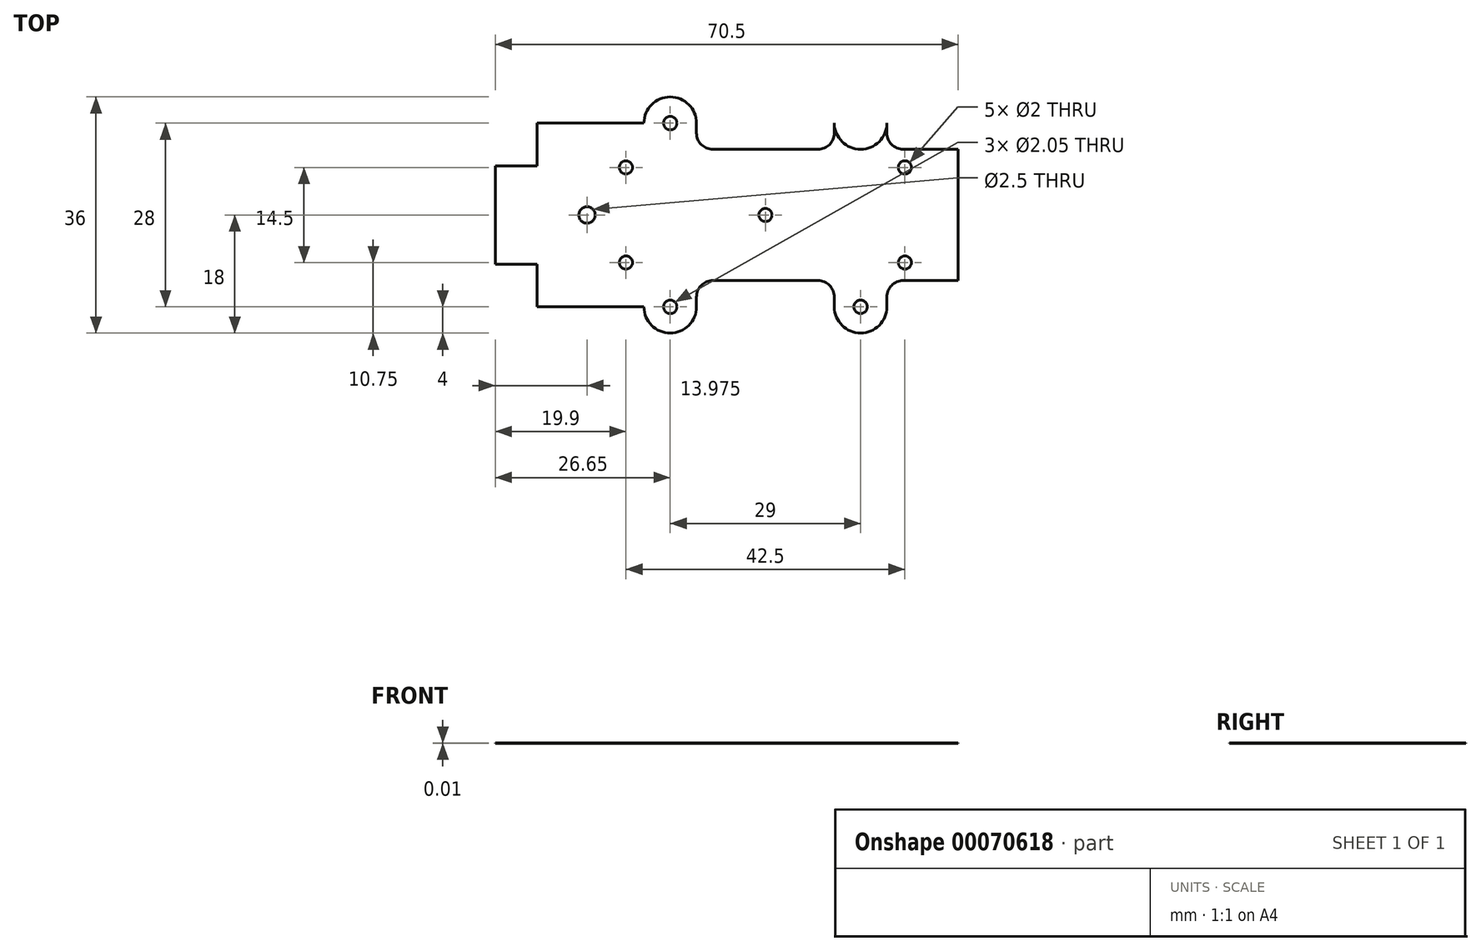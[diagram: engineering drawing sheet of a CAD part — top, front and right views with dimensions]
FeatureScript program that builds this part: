
annotation { "Feature Type Name" : "Feature", "Feature Type Description" : "" }
export const myFeature = defineFeature(function(context is Context, id is Id, definition is map)
    precondition{}
    {
        {
            var Q0;
            Q0=qCreatedBy(makeId("Top.planeOp"),FACE);
            var sketch = newSketch(context, id + "F0", { "sketchPlane" : qUnion([Q0])});
            skLineSegment(sketch, "E0.bottom", {"start": v(-34.8, 10) * mm, "end": v(29.35, 10) * mm});
            skLineSegment(sketch, "E0.top", {"start": v(-34.8, -10) * mm, "end": v(29.35, -10) * mm});
            skLineSegment(sketch, "E0.left", {"start": v(-34.8, 10) * mm, "end": v(-34.8, -10) * mm});
            skLineSegment(sketch, "E0.right", {"start": v(29.35, 10) * mm, "end": v(29.35, -10) * mm});
            skLineSegment(sketch, "E1.bottom", {"start": v(-41.15, 7.5) * mm, "end": v(-34.8, 7.5) * mm});
            skLineSegment(sketch, "E1.top", {"start": v(-41.15, -7.5) * mm, "end": v(-34.8, -7.5) * mm});
            skLineSegment(sketch, "E1.left", {"start": v(-41.15, 7.5) * mm, "end": v(-41.15, -7.5) * mm});
            skLineSegment(sketch, "E1.right", {"start": v(-34.8, 7.5) * mm, "end": v(-34.8, -7.5) * mm});
            skCircle(sketch, "E2", {"center": v(-14.5, 14) * mm, "radius": 4 * mm});
            skLineSegment(sketch, "E3", {"start": v(-18.5, 14) * mm, "end": v(-10.5, 14) * mm});
            skLineSegment(sketch, "E4.top", {"start": v(-18.5, 10) * mm, "end": v(-10.5, 10) * mm});
            skLineSegment(sketch, "E4.left", {"start": v(-18.5, 14) * mm, "end": v(-18.5, 10) * mm});
            skLineSegment(sketch, "E4.right", {"start": v(-10.5, 14) * mm, "end": v(-10.5, 10) * mm});
            skLineSegment(sketch, "E5.MirrorCS", {"start": v(18.5, 14) * mm, "end": v(18.5, 10) * mm});
            skLineSegment(sketch, "E6.MirrorCS", {"start": v(10.5, 14) * mm, "end": v(10.5, 10) * mm});
            skLineSegment(sketch, "E7.MirrorCS", {"start": v(18.5, 10) * mm, "end": v(10.5, 10) * mm});
            skCircle(sketch, "E8.MirrorC", {"center": v(14.5, 14) * mm, "radius": 4 * mm});
            skCircle(sketch, "E9.MirrorC", {"center": v(14.5, -14) * mm, "radius": 4 * mm});
            skLineSegment(sketch, "E10.MirrorCS", {"start": v(18.5, -14) * mm, "end": v(18.5, -10) * mm});
            skLineSegment(sketch, "E11.MirrorCS", {"start": v(10.5, -14) * mm, "end": v(10.5, -10) * mm});
            skLineSegment(sketch, "E12.MirrorCS", {"start": v(-18.5, -10) * mm, "end": v(-10.5, -10) * mm});
            skLineSegment(sketch, "E13.MirrorCS", {"start": v(-10.5, -14) * mm, "end": v(-10.5, -10) * mm});
            skCircle(sketch, "E14.MirrorC", {"center": v(-14.5, -14) * mm, "radius": 4 * mm});
            skPoint(sketch, "E15", {"position": v(-27.18, 0) * mm});
            skLineSegment(sketch, "E16.right", {"start": v(-18.5, -10) * mm, "end": v(-18.5, -14) * mm});
            skLineSegment(sketch, "E17.bottom", {"start": v(-34.8, -10) * mm, "end": v(-11.8, -10) * mm});
            skPoint(sketch, "E18", {"position": v(21.25, 7.25) * mm});
            skPoint(sketch, "E19.MirrorP", {"position": v(21.25, -7.25) * mm});
            skPoint(sketch, "E20.MirrorP", {"position": v(-21.25, -7.25) * mm});
            skPoint(sketch, "E21.MirrorP", {"position": v(-21.25, 7.25) * mm});
            skPoint(sketch, "E22", {"position": v(0, 0) * mm});
            skLineSegment(sketch, "E23", {"start": v(-18.5, 14) * mm, "end": v(-34.8, 14) * mm});
            skLineSegment(sketch, "E24", {"start": v(-34.8, 14) * mm, "end": v(-34.8, 10) * mm});
            skLineSegment(sketch, "E25", {"start": v(-18.5, -14) * mm, "end": v(-34.8, -14) * mm});
            skLineSegment(sketch, "E26", {"start": v(-34.8, -14) * mm, "end": v(-34.8, -10) * mm});
            skSolve(sketch);
        }
        {
            var Q0;
            Q0=makeQuery(id+"F0.imprint","IMPRINT",FACE,{"disambiguationData":[TD([[makeQuery(id+"F0.imprint","IMPRINT",EDGE,{"derivedFrom":sQuery(id+"F0.wireOp",EDGE,"E0.bottom")}),-1.0]])]});
            var Q1;
            Q1=makeQuery(id+"F0.imprint","IMPRINT",FACE,{"disambiguationData":[TD([[makeQuery(id+"F0.imprint","IMPRINT",EDGE,{"derivedFrom":sQuery(id+"F0.wireOp",EDGE,"E1.bottom")}),-1.0]])]});
            var Q2;
            {var subQ0=sQuery(id+"F0.wireOp",EDGE,"E4.left");Q2=makeQuery(id+"F0.imprint","IMPRINT",FACE,{"disambiguationData":[TD([[makeQuery(id+"F0.imprint","IMPRINT",EDGE,{"derivedFrom":subQ0}),1.0]])]});}
            var Q3;
            {var subQ0=sQuery(id+"F0.wireOp",EDGE,"E4.right");Q3=makeQuery(id+"F0.imprint","IMPRINT",FACE,{"disambiguationData":[TD([[makeQuery(id+"F0.imprint","IMPRINT",EDGE,{"derivedFrom":subQ0}),-1.0]])]});}
            var Q4;
            {var subQ0=sQuery(id+"F0.wireOp",EDGE,"E3");Q4=makeQuery(id+"F0.imprint","IMPRINT",FACE,{"disambiguationData":[TD([[makeQuery(id+"F0.imprint","IMPRINT",EDGE,{"derivedFrom":subQ0}),-1.0]])]});}
            var Q5;
            {var subQ0=sQuery(id+"F0.wireOp",EDGE,"E3");Q5=makeQuery(id+"F0.imprint","IMPRINT",FACE,{"disambiguationData":[TD([[makeQuery(id+"F0.imprint","IMPRINT",EDGE,{"derivedFrom":subQ0}),1.0]])]});}
            var Q6;
            {var subQ0=sQuery(id+"F0.wireOp",EDGE,"E6.MirrorCS");Q6=makeQuery(id+"F0.imprint","IMPRINT",FACE,{"disambiguationData":[TD([[makeQuery(id+"F0.imprint","IMPRINT",EDGE,{"derivedFrom":subQ0}),1.0]])]});}
            var Q7;
            {var subQ0=sQuery(id+"F0.wireOp",EDGE,"E8.MirrorC");var subQ1=makeQuery(id+"F0.imprint","INTERSECT",VERTEX,{"derivedFrom":[sQuery(id+"F0.wireOp",EDGE,"E5.MirrorCS"),subQ0]});Q7=makeQuery(id+"F0.imprint","IMPRINT",FACE,{"disambiguationData":[TD([[makeQuery(id+"F0.imprint","IMPRINT",EDGE,{"disambiguationData":[TD([[subQ1,1.0]])],"derivedFrom":subQ0}),-1.0]])]});}
            var Q8;
            {var subQ0=sQuery(id+"F0.wireOp",EDGE,"E5.MirrorCS");Q8=makeQuery(id+"F0.imprint","IMPRINT",FACE,{"disambiguationData":[TD([[makeQuery(id+"F0.imprint","IMPRINT",EDGE,{"derivedFrom":subQ0}),-1.0]])]});}
            var Q9;
            {var subQ0=sQuery(id+"F0.wireOp",EDGE,"E9.MirrorC");var subQ1=makeQuery(id+"F0.imprint","INTERSECT",VERTEX,{"derivedFrom":[subQ0,sQuery(id+"F0.wireOp",EDGE,"E10.MirrorCS")]});Q9=makeQuery(id+"F0.imprint","IMPRINT",FACE,{"disambiguationData":[TD([[makeQuery(id+"F0.imprint","IMPRINT",EDGE,{"disambiguationData":[TD([[subQ1,1.0]])],"derivedFrom":subQ0}),1.0]])]});}
            var Q10;
            {var subQ0=sQuery(id+"F0.wireOp",EDGE,"E10.MirrorCS");Q10=makeQuery(id+"F0.imprint","IMPRINT",FACE,{"disambiguationData":[TD([[makeQuery(id+"F0.imprint","IMPRINT",EDGE,{"derivedFrom":subQ0}),1.0]])]});}
            var Q11;
            {var subQ0=sQuery(id+"F0.wireOp",EDGE,"E11.MirrorCS");Q11=makeQuery(id+"F0.imprint","IMPRINT",FACE,{"disambiguationData":[TD([[makeQuery(id+"F0.imprint","IMPRINT",EDGE,{"derivedFrom":subQ0}),-1.0]])]});}
            var Q12;
            {var subQ0=sQuery(id+"F0.wireOp",EDGE,"E14.MirrorC");var subQ1=makeQuery(id+"F0.imprint","INTERSECT",VERTEX,{"derivedFrom":[sQuery(id+"F0.wireOp",EDGE,"E13.MirrorCS"),subQ0]});Q12=makeQuery(id+"F0.imprint","IMPRINT",FACE,{"disambiguationData":[TD([[makeQuery(id+"F0.imprint","IMPRINT",EDGE,{"disambiguationData":[TD([[subQ1,-1.0]])],"derivedFrom":subQ0}),-1.0]])]});}
            var Q13;
            {var subQ0=sQuery(id+"F0.wireOp",EDGE,"3788546f-e45c-4ba9-8d3c-dabaf8aeedce5.MirrorCS");Q13=makeQuery(id+"F0.imprint","IMPRINT",FACE,{"disambiguationData":[TD([[makeQuery(id+"F0.imprint","IMPRINT",EDGE,{"derivedFrom":subQ0}),-1.0]])]});}
            var Q14;
            {var subQ0=sQuery(id+"F0.wireOp",EDGE,"E13.MirrorCS");Q14=makeQuery(id+"F0.imprint","IMPRINT",FACE,{"disambiguationData":[TD([[makeQuery(id+"F0.imprint","IMPRINT",EDGE,{"derivedFrom":subQ0}),1.0]])]});}
            var Q15;
            Q15=makeQuery(id+"F0.imprint","IMPRINT",FACE,{"disambiguationData":[TD([[makeQuery(id+"F0.imprint","IMPRINT",EDGE,{"derivedFrom":sQuery(id+"F0.wireOp",EDGE,"lHvgetkT-IzEV-z9ZP-LFpq-m1WwzQ1J8MKN.bottom")}),1.0]])]});
            var Q16;
            Q16=makeQuery(id+"F0.imprint","IMPRINT",FACE,{"disambiguationData":[TD([[makeQuery(id+"F0.imprint","IMPRINT",EDGE,{"derivedFrom":sQuery(id+"F0.wireOp",EDGE,"E16.bottom")}),-1.0]])]});
            var Q17;
            {var subQ0=sQuery(id+"F0.wireOp",EDGE,"E16.right");Q17=makeQuery(id+"F0.imprint","IMPRINT",FACE,{"disambiguationData":[TD([[makeQuery(id+"F0.imprint","IMPRINT",EDGE,{"derivedFrom":subQ0}),1.0]])]});}
            var Q18;
            {var subQ0=sQuery(id+"F0.wireOp",EDGE,"E4.left");Q18=makeQuery(id+"F0.imprint","IMPRINT",FACE,{"disambiguationData":[TD([[makeQuery(id+"F0.imprint","IMPRINT",EDGE,{"derivedFrom":subQ0}),1.0]])]});}
            var Q19;
            {var subQ5=sQuery(id+"F0.wireOp",EDGE,"E4.left");Q19=makeQuery(id+"F0.imprint","IMPRINT",FACE,{"disambiguationData":[TD([[makeQuery(id+"F0.imprint","IMPRINT",EDGE,{"derivedFrom":subQ5}),-1.0]])]});}
            var Q20;
            {var subQ0=sQuery(id+"F0.wireOp",EDGE,"E2");var subQ5=makeQuery(id+"F0.imprint","INTERSECT",VERTEX,{"derivedFrom":[sQuery(id+"F0.wireOp",EDGE,"E4.top"),subQ0]});Q20=makeQuery(id+"F0.imprint","IMPRINT",FACE,{"disambiguationData":[TD([[makeQuery(id+"F0.imprint","IMPRINT",EDGE,{"disambiguationData":[TD([[subQ5,1.0]])],"derivedFrom":subQ0}),1.0]])]});}
            var Q21;
            {var subQ1=sQuery(id+"F0.wireOp",EDGE,"E4.top");var subQ3=sQuery(id+"F0.wireOp",EDGE,"E2");var subQ4=makeQuery(id+"F0.imprint","INTERSECT",VERTEX,{"derivedFrom":[subQ1,subQ3]});Q21=makeQuery(id+"F0.imprint","IMPRINT",FACE,{"disambiguationData":[TD([[makeQuery(id+"F0.imprint","IMPRINT",EDGE,{"disambiguationData":[TD([[subQ4,1.0]])],"derivedFrom":subQ3}),-1.0]])]});}
            var Q22;
            {var subQ0=sQuery(id+"F0.wireOp",EDGE,"E14.MirrorC");var subQ1=makeQuery(id+"F0.imprint","INTERSECT",VERTEX,{"derivedFrom":[subQ0,sQuery(id+"F0.wireOp",EDGE,"E16.right")]});Q22=makeQuery(id+"F0.imprint","IMPRINT",FACE,{"disambiguationData":[TD([[makeQuery(id+"F0.imprint","IMPRINT",EDGE,{"disambiguationData":[TD([[subQ1,1.0]])],"derivedFrom":subQ0}),-1.0]])]});}
            var Q23;
            {var subQ0=sQuery(id+"F0.wireOp",EDGE,"E16.right");Q23=makeQuery(id+"F0.imprint","IMPRINT",FACE,{"disambiguationData":[TD([[makeQuery(id+"F0.imprint","IMPRINT",EDGE,{"derivedFrom":subQ0}),-1.0]])]});}
            var Q24;
            {var subQ1=sQuery(id+"F0.wireOp",EDGE,"E12.MirrorCS");var subQ3=sQuery(id+"F0.wireOp",EDGE,"E14.MirrorC");var subQ4=makeQuery(id+"F0.imprint","INTERSECT",VERTEX,{"derivedFrom":[subQ1,subQ3]});Q24=makeQuery(id+"F0.imprint","IMPRINT",FACE,{"disambiguationData":[TD([[makeQuery(id+"F0.imprint","IMPRINT",EDGE,{"disambiguationData":[TD([[subQ4,1.0]])],"derivedFrom":subQ3}),1.0]])]});}
            extrude(context, id + "F1", {"entities" : qUnion([Q0, Q1, Q2, Q3, Q4, Q5, Q6, Q7, Q8, Q9, Q10, Q11, Q12, Q13, Q14, Q15, Q16, Q17, Q18, Q19, Q20, Q21, Q22, Q23, Q24]), "depth" : 1 / 101.6 * mm});
        }
        {
            var Q0;
            Q0=sQuery(id+"F0.wireOp",VERTEX,"E2.center");
            var Q1;
            Q1=sQuery(id+"F0.wireOp",VERTEX,"E8.MirrorC.center");
            var Q2;
            Q2=sQuery(id+"F0.wireOp",VERTEX,"E9.MirrorC.center");
            var Q3;
            Q3=sQuery(id+"F0.wireOp",VERTEX,"E14.MirrorC.center");
            var Q4;
            Q4=makeQuery(id+"F1.opExtrude","SWEPT_BODY",BODY,{"disambiguationData":[OSD([sQuery(id+"F0.wireOp",EDGE,"E0.bottom"),sQuery(id+"F0.wireOp",EDGE,"E0.top"),sQuery(id+"F0.wireOp",EDGE,"E0.left"),sQuery(id+"F0.wireOp",EDGE,"E0.right"),sQuery(id+"F0.wireOp",EDGE,"E1.bottom"),sQuery(id+"F0.wireOp",EDGE,"E1.top"),sQuery(id+"F0.wireOp",EDGE,"E1.left"),sQuery(id+"F0.wireOp",EDGE,"E4.right"),sQuery(id+"F0.wireOp",EDGE,"E5.MirrorCS"),sQuery(id+"F0.wireOp",EDGE,"E6.MirrorCS"),sQuery(id+"F0.wireOp",EDGE,"E8.MirrorC"),sQuery(id+"F0.wireOp",EDGE,"E2"),sQuery(id+"F0.wireOp",EDGE,"E4.left"),sQuery(id+"F0.wireOp",EDGE,"E9.MirrorC"),sQuery(id+"F0.wireOp",EDGE,"E10.MirrorCS"),sQuery(id+"F0.wireOp",EDGE,"E11.MirrorCS"),sQuery(id+"F0.wireOp",EDGE,"E13.MirrorCS"),sQuery(id+"F0.wireOp",EDGE,"3788546f-e45c-4ba9-8d3c-dabaf8aeedce5.MirrorCS"),sQuery(id+"F0.wireOp",EDGE,"E14.MirrorC")])]});
            hole(context, id + "F2", {"style" : HoleStyle.SIMPLE, "endStyle" : HoleEndStyle.THROUGH, "oppositeDirection" : true, "holeDiameter" : 2.05 * mm, "locations" : qUnion([Q0, Q1, Q2, Q3]), "scope" : qUnion([Q4]), "isTappedThrough" : true});
        }
        {
            var Q0;
            Q0=sQuery(id+"F0.wireOp",VERTEX,"E15");
            var Q1;
            Q1=makeQuery(id+"F1.opExtrude","SWEPT_BODY",BODY,{"disambiguationData":[OSD([sQuery(id+"F0.wireOp",EDGE,"E0.bottom"),sQuery(id+"F0.wireOp",EDGE,"E0.top"),sQuery(id+"F0.wireOp",EDGE,"E0.left"),sQuery(id+"F0.wireOp",EDGE,"E0.right"),sQuery(id+"F0.wireOp",EDGE,"E1.bottom"),sQuery(id+"F0.wireOp",EDGE,"E1.top"),sQuery(id+"F0.wireOp",EDGE,"E1.left"),sQuery(id+"F0.wireOp",EDGE,"E4.right"),sQuery(id+"F0.wireOp",EDGE,"E5.MirrorCS"),sQuery(id+"F0.wireOp",EDGE,"E6.MirrorCS"),sQuery(id+"F0.wireOp",EDGE,"E8.MirrorC"),sQuery(id+"F0.wireOp",EDGE,"E2"),sQuery(id+"F0.wireOp",EDGE,"E4.left"),sQuery(id+"F0.wireOp",EDGE,"E9.MirrorC"),sQuery(id+"F0.wireOp",EDGE,"E10.MirrorCS"),sQuery(id+"F0.wireOp",EDGE,"E11.MirrorCS"),sQuery(id+"F0.wireOp",EDGE,"E13.MirrorCS"),sQuery(id+"F0.wireOp",EDGE,"3788546f-e45c-4ba9-8d3c-dabaf8aeedce5.MirrorCS"),sQuery(id+"F0.wireOp",EDGE,"E14.MirrorC")])]});
            hole(context, id + "F3", {"style" : HoleStyle.SIMPLE, "endStyle" : HoleEndStyle.THROUGH, "oppositeDirection" : true, "holeDiameter" : 2.5 * mm, "locations" : qUnion([Q0]), "scope" : qUnion([Q1]), "isTappedThrough" : true});
        }
        {
            var Q0;
            Q0=makeQuery(id+"F1.opExtrude","SWEPT_EDGE",EDGE,{"disambiguationData":[OSD([sQuery(id+"F0.wireOp",EDGE,"E0.bottom"),sQuery(id+"F0.wireOp",EDGE,"E4.top"),sQuery(id+"F0.wireOp",EDGE,"E4.right")])]});
            var Q1;
            Q1=makeQuery(id+"F1.opExtrude","SWEPT_EDGE",EDGE,{"disambiguationData":[OSD([sQuery(id+"F0.wireOp",EDGE,"E0.bottom"),sQuery(id+"F0.wireOp",EDGE,"E6.MirrorCS"),sQuery(id+"F0.wireOp",EDGE,"E7.MirrorCS")])]});
            var Q2;
            Q2=makeQuery(id+"F1.opExtrude","SWEPT_EDGE",EDGE,{"disambiguationData":[OSD([sQuery(id+"F0.wireOp",EDGE,"E0.bottom"),sQuery(id+"F0.wireOp",EDGE,"E5.MirrorCS"),sQuery(id+"F0.wireOp",EDGE,"E7.MirrorCS")])]});
            var Q3;
            Q3=makeQuery(id+"F1.opExtrude","SWEPT_EDGE",EDGE,{"disambiguationData":[OSD([sQuery(id+"F0.wireOp",EDGE,"E0.top"),sQuery(id+"F0.wireOp",EDGE,"E12.MirrorCS"),sQuery(id+"F0.wireOp",EDGE,"E13.MirrorCS")])]});
            var Q4;
            Q4=makeQuery(id+"F1.opExtrude","SWEPT_EDGE",EDGE,{"disambiguationData":[OSD([sQuery(id+"F0.wireOp",EDGE,"E0.top"),sQuery(id+"F0.wireOp",EDGE,"E11.MirrorCS")])]});
            var Q5;
            Q5=makeQuery(id+"F1.opExtrude","SWEPT_EDGE",EDGE,{"disambiguationData":[OSD([sQuery(id+"F0.wireOp",EDGE,"E0.top"),sQuery(id+"F0.wireOp",EDGE,"E10.MirrorCS")])]});
            var Q6;
            Q6=makeQuery(id+"F1.opExtrude","SWEPT_EDGE",EDGE,{"disambiguationData":[OSD([sQuery(id+"F0.wireOp",EDGE,"E2"),sQuery(id+"F0.wireOp",EDGE,"iMMn4YZA-4PE5-njVe-fSwm-rbs8x8JU8x5A.top")])]});
            fillet(context, id + "F4", {"entities" : qUnion([Q0, Q1, Q2, Q3, Q4, Q5, Q6]), "radius" : 2.5 * mm, "tangentPropagation" : true, "allowEdgeOverflow" : false});
        }
        {
            var Q0;
            Q0=makeQuery(id+"F1.opExtrude","SWEPT_FACE",FACE,{"disambiguationData":[OSD([sQuery(id+"F0.wireOp",EDGE,"E0.left"),sQuery(id+"F0.wireOp",EDGE,"E17.left")])]});
            var sketch = newSketch(context, id + "F5", { "sketchPlane" : qUnion([Q0])});
            skPoint(sketch, "E27", {"position": v(11.25, 3.18) * mm});
            skSolve(sketch);
        }
        {
            var Q0;
            Q0=makeQuery(id+"F1.opExtrude","SWEPT_FACE",FACE,{"disambiguationData":[OSD([sQuery(id+"F0.wireOp",EDGE,"E0.left"),sQuery(id+"F0.wireOp",EDGE,"iMMn4YZA-4PE5-njVe-fSwm-rbs8x8JU8x5A.left")])]});
            var sketch = newSketch(context, id + "F6", { "sketchPlane" : qUnion([Q0])});
            skPoint(sketch, "E28", {"position": v(-11.25, 3.17) * mm});
            skSolve(sketch);
        }
        {
            var Q0;
            Q0=sQuery(id+"F6.wireOp",VERTEX,"E28");
            var Q1;
            Q1=sQuery(id+"F5.wireOp",VERTEX,"E27");
            var Q2;
            Q2=makeQuery(id+"F1.opExtrude","SWEPT_BODY",BODY,{"disambiguationData":[OSD([sQuery(id+"F0.wireOp",EDGE,"E0.bottom"),sQuery(id+"F0.wireOp",EDGE,"E0.top"),sQuery(id+"F0.wireOp",EDGE,"E0.left"),sQuery(id+"F0.wireOp",EDGE,"E0.right"),sQuery(id+"F0.wireOp",EDGE,"E1.bottom"),sQuery(id+"F0.wireOp",EDGE,"E1.top"),sQuery(id+"F0.wireOp",EDGE,"E1.left"),sQuery(id+"F0.wireOp",EDGE,"E4.right"),sQuery(id+"F0.wireOp",EDGE,"E5.MirrorCS"),sQuery(id+"F0.wireOp",EDGE,"E6.MirrorCS"),sQuery(id+"F0.wireOp",EDGE,"E8.MirrorC"),sQuery(id+"F0.wireOp",EDGE,"E2"),sQuery(id+"F0.wireOp",EDGE,"E9.MirrorC"),sQuery(id+"F0.wireOp",EDGE,"E10.MirrorCS"),sQuery(id+"F0.wireOp",EDGE,"E11.MirrorCS"),sQuery(id+"F0.wireOp",EDGE,"E13.MirrorCS"),sQuery(id+"F0.wireOp",EDGE,"E14.MirrorC"),sQuery(id+"F0.wireOp",EDGE,"iMMn4YZA-4PE5-njVe-fSwm-rbs8x8JU8x5A.top"),sQuery(id+"F0.wireOp",EDGE,"iMMn4YZA-4PE5-njVe-fSwm-rbs8x8JU8x5A.left"),sQuery(id+"F0.wireOp",EDGE,"E17.top"),sQuery(id+"F0.wireOp",EDGE,"E17.left")])]});
            hole(context, id + "F7", {"style" : HoleStyle.SIMPLE, "endStyle" : HoleEndStyle.BLIND, "holeDiameter" : 2.05 * mm, "holeDepth" : 6 * mm, "locations" : qUnion([Q0, Q1]), "scope" : qUnion([Q2])});
        }
        {
            var Q0;
            Q0=sQuery(id+"F0.wireOp",VERTEX,"E21.MirrorP");
            var Q1;
            Q1=sQuery(id+"F0.wireOp",VERTEX,"E20.MirrorP");
            var Q2;
            Q2=sQuery(id+"F0.wireOp",VERTEX,"E22");
            var Q3;
            Q3=sQuery(id+"F0.wireOp",VERTEX,"E18");
            var Q4;
            Q4=sQuery(id+"F0.wireOp",VERTEX,"E19.MirrorP");
            var Q5;
            Q5=makeQuery(id+"F1.opExtrude","SWEPT_BODY",BODY,{"disambiguationData":[OSD([sQuery(id+"F0.wireOp",EDGE,"E0.bottom"),sQuery(id+"F0.wireOp",EDGE,"E0.top"),sQuery(id+"F0.wireOp",EDGE,"E0.left"),sQuery(id+"F0.wireOp",EDGE,"E0.right"),sQuery(id+"F0.wireOp",EDGE,"E1.bottom"),sQuery(id+"F0.wireOp",EDGE,"E1.top"),sQuery(id+"F0.wireOp",EDGE,"E1.left"),sQuery(id+"F0.wireOp",EDGE,"E4.right"),sQuery(id+"F0.wireOp",EDGE,"E5.MirrorCS"),sQuery(id+"F0.wireOp",EDGE,"E6.MirrorCS"),sQuery(id+"F0.wireOp",EDGE,"E8.MirrorC"),sQuery(id+"F0.wireOp",EDGE,"E2"),sQuery(id+"F0.wireOp",EDGE,"E9.MirrorC"),sQuery(id+"F0.wireOp",EDGE,"E10.MirrorCS"),sQuery(id+"F0.wireOp",EDGE,"E11.MirrorCS"),sQuery(id+"F0.wireOp",EDGE,"E13.MirrorCS"),sQuery(id+"F0.wireOp",EDGE,"E14.MirrorC"),sQuery(id+"F0.wireOp",EDGE,"iMMn4YZA-4PE5-njVe-fSwm-rbs8x8JU8x5A.top"),sQuery(id+"F0.wireOp",EDGE,"iMMn4YZA-4PE5-njVe-fSwm-rbs8x8JU8x5A.left"),sQuery(id+"F0.wireOp",EDGE,"E17.top"),sQuery(id+"F0.wireOp",EDGE,"E17.left")])]});
            hole(context, id + "F8", {"style" : HoleStyle.SIMPLE, "endStyle" : HoleEndStyle.THROUGH, "oppositeDirection" : true, "holeDiameter" : 2 * mm, "locations" : qUnion([Q0, Q1, Q2, Q3, Q4]), "scope" : qUnion([Q5]), "isTappedThrough" : true});
        }
    });
